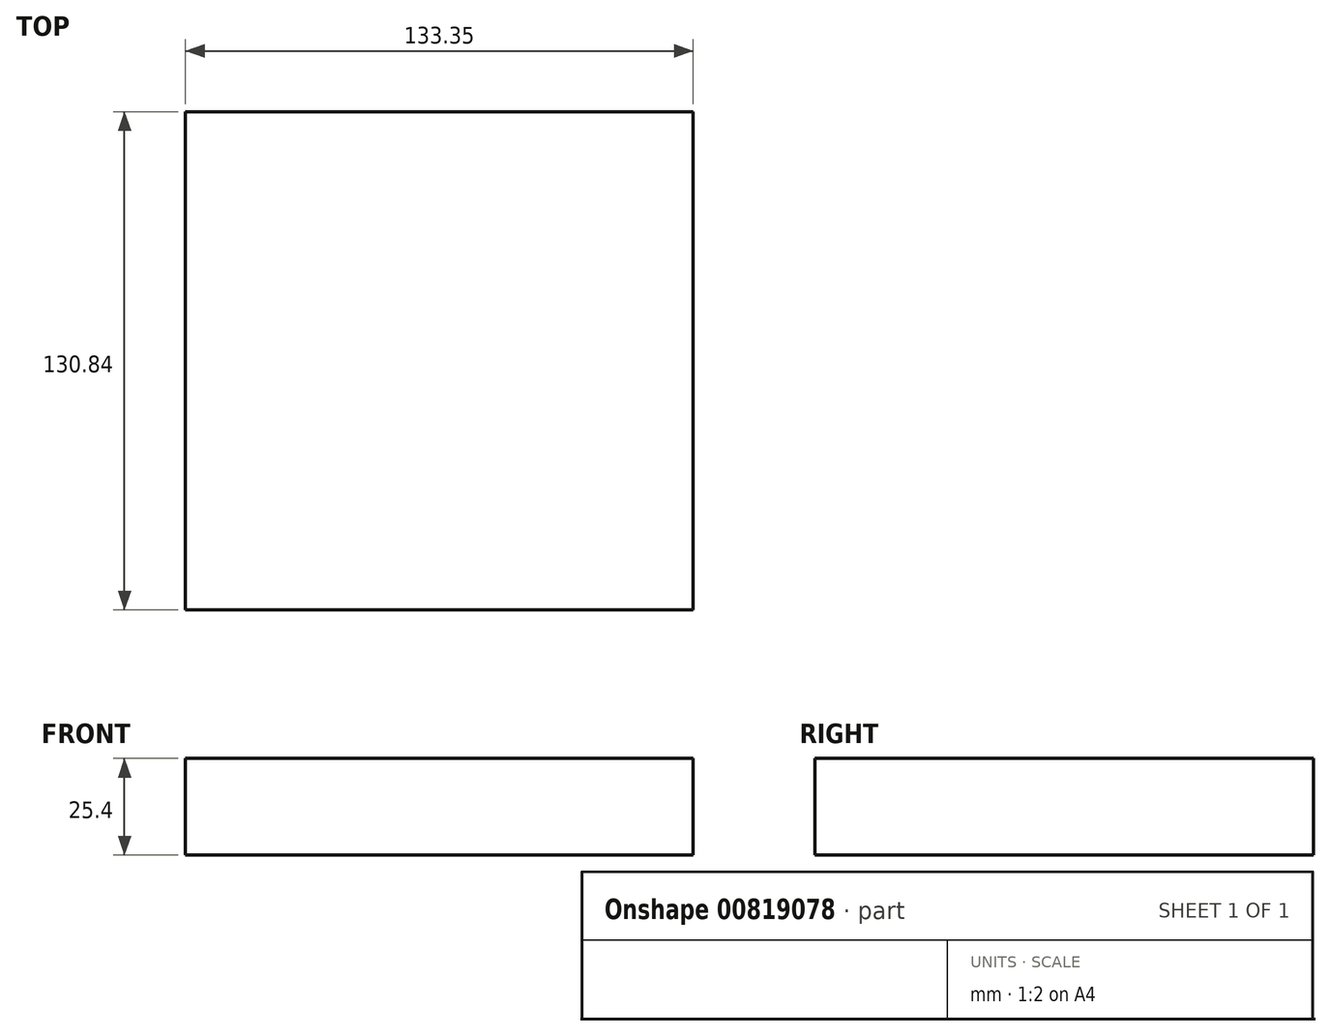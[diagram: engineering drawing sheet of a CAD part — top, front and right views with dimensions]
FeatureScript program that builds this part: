
annotation { "Feature Type Name" : "Feature", "Feature Type Description" : "" }
export const myFeature = defineFeature(function(context is Context, id is Id, definition is map)
    precondition{}
    {
        {
            var Q0;
            Q0=qCreatedBy(makeId("Top.planeOp"),FACE);
            var sketch = newSketch(context, id + "F0", { "sketchPlane" : qUnion([Q0])});
            skLineSegment(sketch, "E0.bottom", {"start": v(81.39, 54.07) * mm, "end": v(214.74, 54.07) * mm});
            skLineSegment(sketch, "E0.top", {"start": v(81.39, -76.77) * mm, "end": v(214.74, -76.77) * mm});
            skLineSegment(sketch, "E0.left", {"start": v(81.39, 54.07) * mm, "end": v(81.39, -76.77) * mm});
            skLineSegment(sketch, "E0.right", {"start": v(214.74, 54.07) * mm, "end": v(214.74, -76.77) * mm});
            skSolve(sketch);
        }
        {
            var Q0;
            Q0=makeQuery(id+"F0.imprint","IMPRINT",FACE,{"disambiguationData":[TD([[makeQuery(id+"F0.imprint","IMPRINT",EDGE,{"derivedFrom":sQuery(id+"F0.wireOp",EDGE,"E0.bottom")}),-1.0]])]});
            extrude(context, id + "F1", {"entities" : qUnion([Q0]), "depth" : 25.4 * mm, "offsetDistance" : 25.4 * mm});
        }
    });
